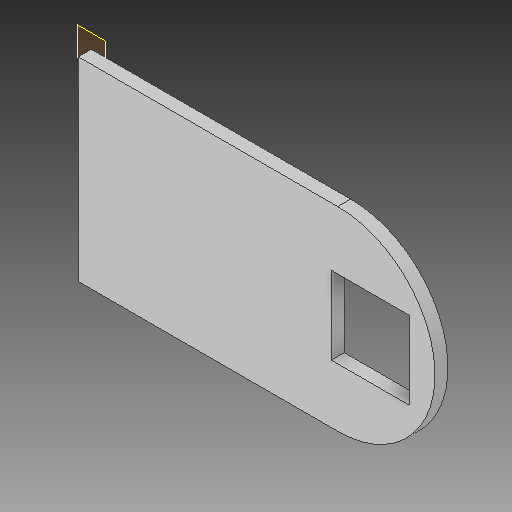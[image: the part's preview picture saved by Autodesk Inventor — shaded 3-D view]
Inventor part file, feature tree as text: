
AUTODESK INVENTOR PART (.ipt)
format: ipt  version: 2018.3 (Build 223284000, 284)  size: 109,568 bytes
history: native  units: mm
features: other x1, extrude x1, sketch x1
ambient origin geometry x8: Origin, YZ Plane, XZ Plane, XY Plane, X Axis, Y Axis, Z Axis, Center Point
bodies: Body1 (feature_tree)
feature tree (3):
  other  "РабПлоскость1"
  extrude  "Выдавливание1"  Depth=60.0mm
  sketch  "Эскиз1"
